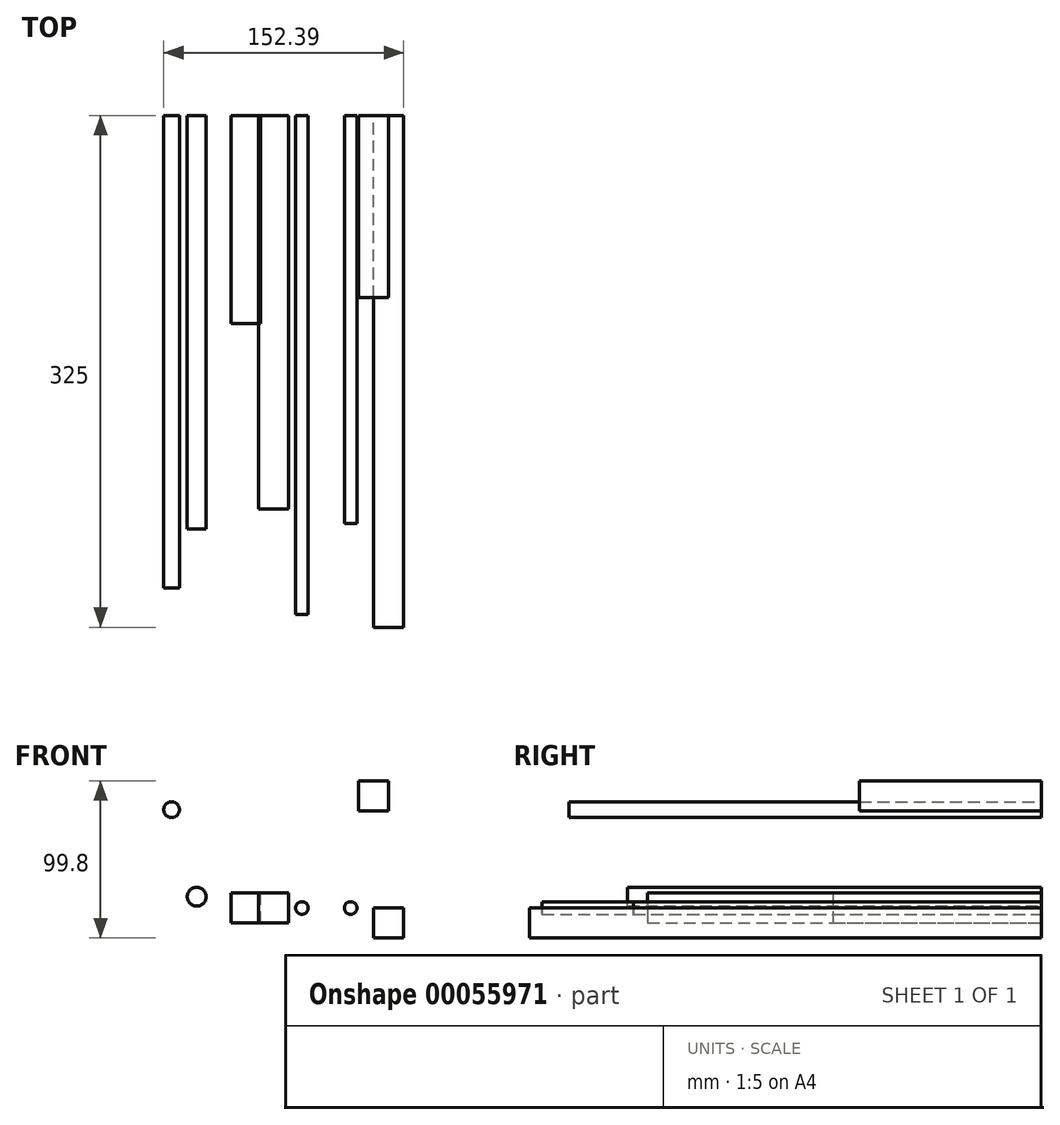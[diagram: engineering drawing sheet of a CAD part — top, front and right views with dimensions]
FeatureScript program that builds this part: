
annotation { "Feature Type Name" : "Feature", "Feature Type Description" : "" }
export const myFeature = defineFeature(function(context is Context, id is Id, definition is map)
    precondition{}
    {
        {
            var Q0;
            Q0=qCreatedBy(makeId("Front.planeOp"),FACE);
            var sketch = newSketch(context, id + "F0", { "sketchPlane" : qUnion([Q0])});
            skLineSegment(sketch, "E0.rect.bottom", {"start": v(9.5, 9.5) * mm, "end": v(-9.5, 9.5) * mm});
            skLineSegment(sketch, "E0.rect.top", {"start": v(9.5, -9.5) * mm, "end": v(-9.5, -9.5) * mm});
            skLineSegment(sketch, "E0.rect.left", {"start": v(9.5, 9.5) * mm, "end": v(9.5, -9.5) * mm});
            skLineSegment(sketch, "E0.rect.right", {"start": v(-9.5, 9.5) * mm, "end": v(-9.5, -9.5) * mm});
            skPoint(sketch, "E0.rect.middle", {"position": v(0, 0) * mm});
            skSolve(sketch);
        }
        {
            var Q0;
            Q0=makeQuery(id+"F0.imprint","IMPRINT",FACE,{"disambiguationData":[TD([[makeQuery(id+"F0.imprint","IMPRINT",EDGE,{"derivedFrom":sQuery(id+"F0.wireOp",EDGE,"E0.rect.bottom")}),1.0]])]});
            extrude(context, id + "F1", {"entities" : qUnion([Q0]), "depth" : 250 * mm});
        }
        {
            var Q0;
            Q0=qCreatedBy(makeId("Front.planeOp"),FACE);
            var sketch = newSketch(context, id + "F2", { "sketchPlane" : qUnion([Q0])});
            skLineSegment(sketch, "E1.rect.bottom", {"start": v(-27.2, -9.5) * mm, "end": v(-8.2, -9.5) * mm});
            skLineSegment(sketch, "E1.rect.top", {"start": v(-27.2, 9.5) * mm, "end": v(-8.2, 9.5) * mm});
            skLineSegment(sketch, "E1.rect.left", {"start": v(-27.2, -9.5) * mm, "end": v(-27.2, 9.5) * mm});
            skLineSegment(sketch, "E1.rect.right", {"start": v(-8.2, -9.5) * mm, "end": v(-8.2, 9.5) * mm});
            skPoint(sketch, "E1.rect.middle", {"position": v(-17.7, 0) * mm});
            skSolve(sketch);
        }
        {
            var Q0;
            Q0=makeQuery(id+"F2.imprint","IMPRINT",FACE,{"disambiguationData":[TD([[makeQuery(id+"F2.imprint","IMPRINT",EDGE,{"derivedFrom":sQuery(id+"F2.wireOp",EDGE,"E1.rect.bottom")}),1.0]])]});
            extrude(context, id + "F3", {"entities" : qUnion([Q0]), "depth" : 132 * mm});
        }
        {
            var Q0;
            Q0=qCreatedBy(makeId("Front.planeOp"),FACE);
            var sketch = newSketch(context, id + "F4", { "sketchPlane" : qUnion([Q0])});
            skCircle(sketch, "E2", {"center": v(-48.94, 7.18) * mm, "radius": 6 * mm});
            skSolve(sketch);
        }
        {
            var Q0;
            Q0=makeQuery(id+"F4.imprint","IMPRINT",FACE,{"disambiguationData":[TD([[makeQuery(id+"F4.imprint","IMPRINT",EDGE,{"derivedFrom":sQuery(id+"F4.wireOp",EDGE,"E2")}),1.0]])]});
            extrude(context, id + "F5", {"entities" : qUnion([Q0]), "depth" : 262.7 * mm});
        }
        {
            var Q0;
            Q0=qCreatedBy(makeId("Front.planeOp"),FACE);
            var sketch = newSketch(context, id + "F6", { "sketchPlane" : qUnion([Q0])});
            skCircle(sketch, "E3", {"center": v(48.85, 0) * mm, "radius": 4 * mm});
            skSolve(sketch);
        }
        {
            var Q0;
            Q0=makeQuery(id+"F6.imprint","IMPRINT",FACE,{"disambiguationData":[TD([[makeQuery(id+"F6.imprint","IMPRINT",EDGE,{"derivedFrom":sQuery(id+"F6.wireOp",EDGE,"E3")}),1.0]])]});
            extrude(context, id + "F7", {"entities" : qUnion([Q0]), "depth" : 259 * mm});
        }
        {
            var Q0;
            Q0=qCreatedBy(makeId("Front.planeOp"),FACE);
            var sketch = newSketch(context, id + "F8", { "sketchPlane" : qUnion([Q0])});
            skLineSegment(sketch, "E4.bottom", {"start": v(63.5, 0) * mm, "end": v(82.5, 0) * mm});
            skLineSegment(sketch, "E4.top", {"start": v(63.5, -19) * mm, "end": v(82.5, -19) * mm});
            skLineSegment(sketch, "E4.left", {"start": v(63.5, 0) * mm, "end": v(63.5, -19) * mm});
            skLineSegment(sketch, "E4.right", {"start": v(82.5, 0) * mm, "end": v(82.5, -19) * mm});
            skSolve(sketch);
        }
        {
            var Q0;
            Q0=makeQuery(id+"F8.imprint","IMPRINT",FACE,{"disambiguationData":[TD([[makeQuery(id+"F8.imprint","IMPRINT",EDGE,{"derivedFrom":sQuery(id+"F8.wireOp",EDGE,"E4.bottom")}),-1.0]])]});
            extrude(context, id + "F9", {"entities" : qUnion([Q0]), "depth" : 325 * mm});
        }
        {
            var Q0;
            Q0=qCreatedBy(makeId("Front.planeOp"),FACE);
            var sketch = newSketch(context, id + "F10", { "sketchPlane" : qUnion([Q0])});
            skCircle(sketch, "E5", {"center": v(17.89, 0) * mm, "radius": 4 * mm});
            skSolve(sketch);
        }
        {
            var Q0;
            Q0=makeQuery(id+"F10.imprint","IMPRINT",FACE,{"disambiguationData":[TD([[makeQuery(id+"F10.imprint","IMPRINT",EDGE,{"derivedFrom":sQuery(id+"F10.wireOp",EDGE,"E5")}),1.0]])]});
            var Q1;
            Q1=makeQuery(id+"F9.opExtrude","CAP_FACE",FACE,{"disambiguationData":[OSD([sQuery(id+"F8.wireOp",EDGE,"E4.bottom"),sQuery(id+"F8.wireOp",EDGE,"E4.top"),sQuery(id+"F8.wireOp",EDGE,"E4.left"),sQuery(id+"F8.wireOp",EDGE,"E4.right")])],"isStart":false});
            extrude(context, id + "F11", {"entities" : qUnion([Q0]), "endBoundEntityFace" : qUnion([Q1]), "depth" : (325 - 8) * mm});
        }
        {
            var Q0;
            Q0=qCreatedBy(makeId("Front.planeOp"),FACE);
            var sketch = newSketch(context, id + "F12", { "sketchPlane" : qUnion([Q0])});
            skCircle(sketch, "E6", {"center": v(-64.89, 62.45) * mm, "radius": 5 * mm});
            skSolve(sketch);
        }
        {
            var Q0;
            Q0=makeQuery(id+"F12.imprint","IMPRINT",FACE,{"disambiguationData":[TD([[makeQuery(id+"F12.imprint","IMPRINT",EDGE,{"derivedFrom":sQuery(id+"F12.wireOp",EDGE,"E6")}),1.0]])]});
            extrude(context, id + "F13", {"entities" : qUnion([Q0]), "depth" : 300 * mm});
        }
        {
            var Q0;
            Q0=qCreatedBy(makeId("Front.planeOp"),FACE);
            var sketch = newSketch(context, id + "F14", { "sketchPlane" : qUnion([Q0])});
            skLineSegment(sketch, "E7.bottom", {"start": v(53.88, 61.8) * mm, "end": v(72.88, 61.8) * mm});
            skLineSegment(sketch, "E7.top", {"start": v(53.88, 80.8) * mm, "end": v(72.88, 80.8) * mm});
            skLineSegment(sketch, "E7.left", {"start": v(53.88, 61.8) * mm, "end": v(53.88, 80.8) * mm});
            skLineSegment(sketch, "E7.right", {"start": v(72.88, 61.8) * mm, "end": v(72.88, 80.8) * mm});
            skSolve(sketch);
        }
        {
            var Q0;
            Q0=makeQuery(id+"F14.imprint","IMPRINT",FACE,{"disambiguationData":[TD([[makeQuery(id+"F14.imprint","IMPRINT",EDGE,{"derivedFrom":sQuery(id+"F14.wireOp",EDGE,"E7.bottom")}),1.0]])]});
            extrude(context, id + "F15", {"entities" : qUnion([Q0]), "depth" : 115.5 * mm});
        }
    });
